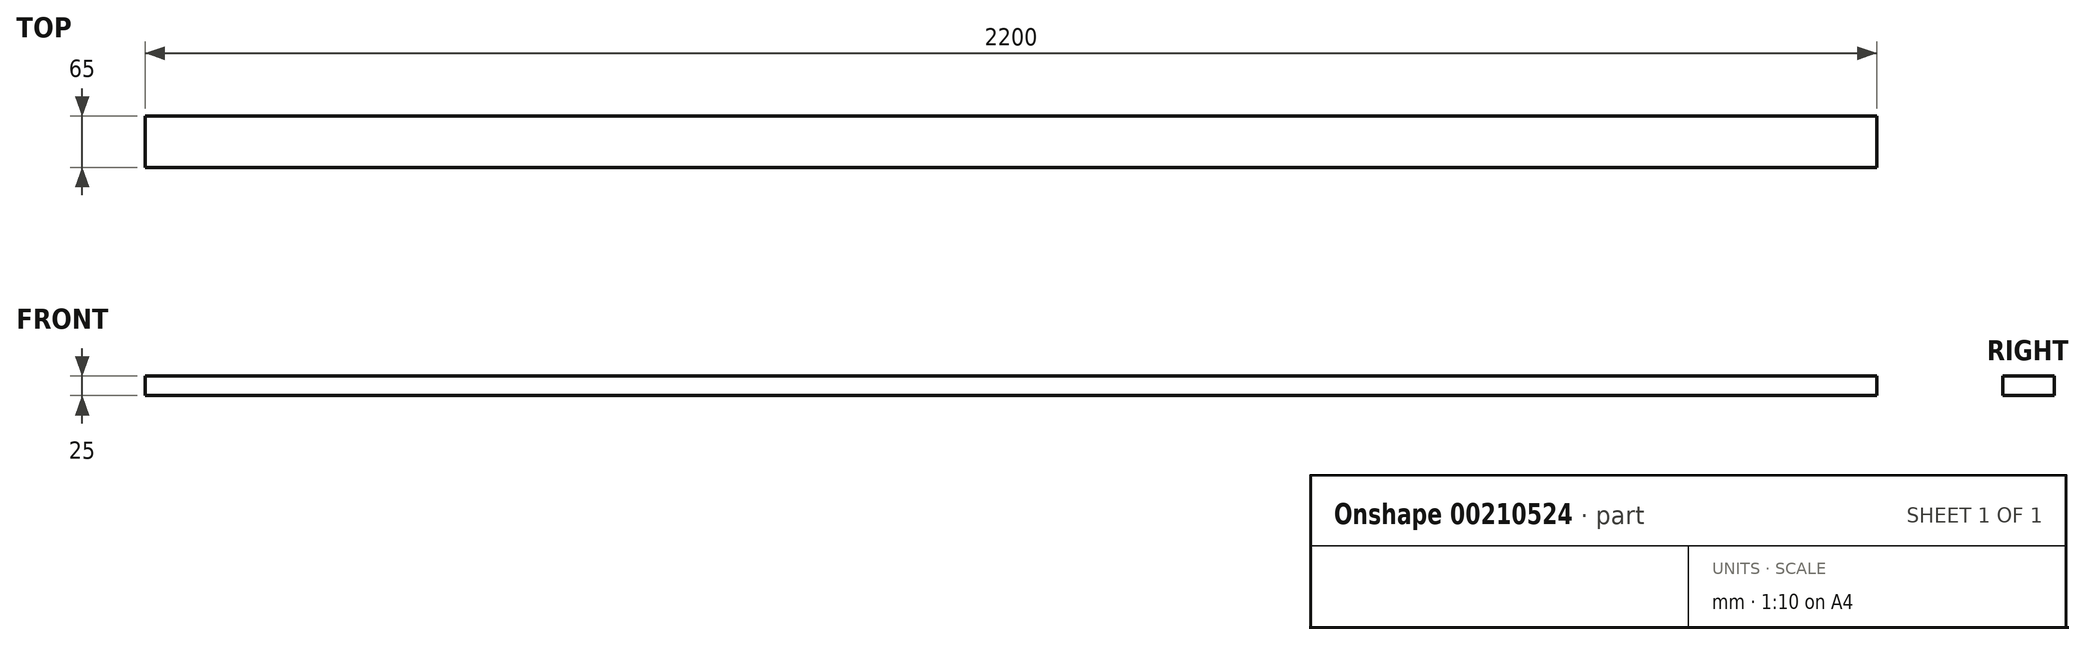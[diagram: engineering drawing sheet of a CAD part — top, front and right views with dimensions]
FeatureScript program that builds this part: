
annotation { "Feature Type Name" : "Feature", "Feature Type Description" : "" }
export const myFeature = defineFeature(function(context is Context, id is Id, definition is map)
    precondition{}
    {
        {
            var Q0;
            Q0=qCreatedBy(makeId("Top.planeOp"),FACE);
            var sketch = newSketch(context, id + "F0", { "sketchPlane" : qUnion([Q0])});
            skLineSegment(sketch, "E0.bottom", {"start": v(-1062.35, -14.28) * mm, "end": v(1137.65, -14.28) * mm});
            skLineSegment(sketch, "E0.top", {"start": v(-1062.35, -79.28) * mm, "end": v(1137.65, -79.28) * mm});
            skLineSegment(sketch, "E0.left", {"start": v(-1062.35, -14.28) * mm, "end": v(-1062.35, -79.28) * mm});
            skLineSegment(sketch, "E0.right", {"start": v(1137.65, -14.28) * mm, "end": v(1137.65, -79.28) * mm});
            skSolve(sketch);
        }
        {
            var Q0;
            Q0 = qSketchRegion(id + "F0", true);
            var Q1;
            Q1=makeQuery(id+"F0.imprint","IMPRINT",FACE,{"disambiguationData":[TD([[makeQuery(id+"F0.imprint","IMPRINT",EDGE,{"derivedFrom":sQuery(id+"F0.wireOp",EDGE,"E0.bottom")}),-1.0]])]});
            extrude(context, id + "F1", {"entities" : qUnion([Q0, Q1]), "depth" : 25 * mm});
        }
    });
